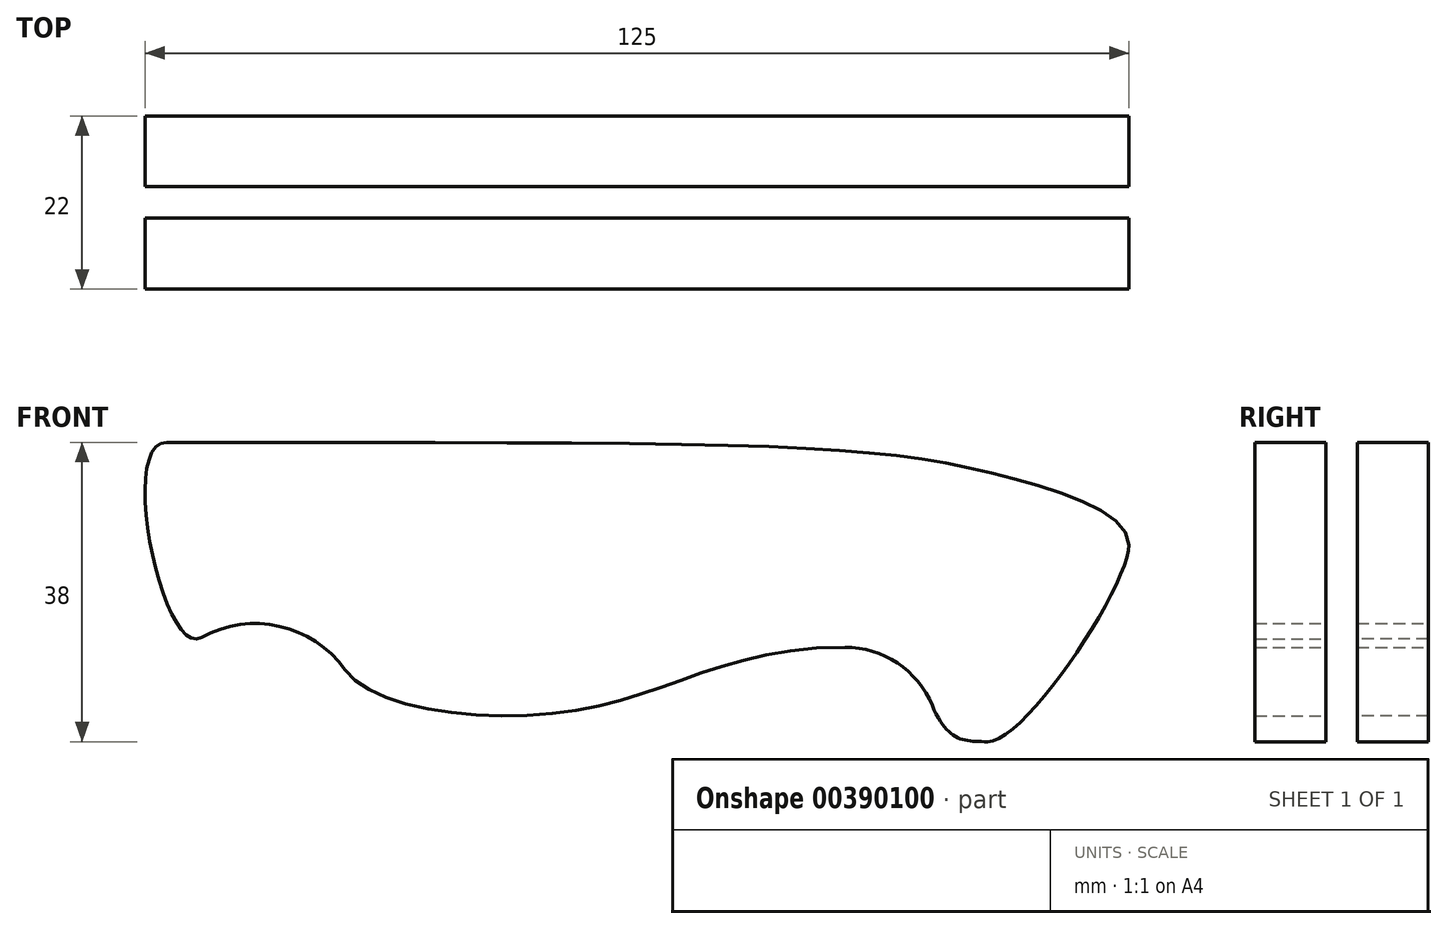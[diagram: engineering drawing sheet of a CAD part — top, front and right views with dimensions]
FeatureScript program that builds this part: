
annotation { "Feature Type Name" : "Feature", "Feature Type Description" : "" }
export const myFeature = defineFeature(function(context is Context, id is Id, definition is map)
    precondition{}
    {
        {
            var Q0;
            Q0=qCreatedBy(makeId("Front.planeOp"),FACE);
            var sketch = newSketch(context, id + "F0", { "sketchPlane" : qUnion([Q0])});
            skLineSegment(sketch, "E0", {"start": v(0, 38) * mm, "end": v(-240, 38) * mm});
            skLineSegment(sketch, "E1", {"start": v(-240, 38) * mm, "end": v(-240, 0) * mm});
            skLineSegment(sketch, "E2", {"start": v(-240, 0) * mm, "end": v(0, 0) * mm});
            skLineSegment(sketch, "E3", {"start": v(0, 0) * mm, "end": v(0, 38) * mm});
            skSolve(sketch);
        }
        {
            var Q0;
            Q0=makeQuery(id+"F0.imprint","IMPRINT",FACE,{"disambiguationData":[TD([[makeQuery(id+"F0.imprint","IMPRINT",EDGE,{"derivedFrom":sQuery(id+"F0.wireOp",EDGE,"E0")}),1.0]])]});
            var sketch = newSketch(context, id + "F1", { "sketchPlane" : qUnion([Q0])});
            skLineSegment(sketch, "E4", {"start": v(0, 50) * mm, "end": v(-125, 50) * mm, "construction": true});
            skLineSegment(sketch, "E5", {"start": v(-125, 50) * mm, "end": v(-240, 50) * mm, "construction": true});
            skLineSegment(sketch, "E6", {"start": v(-125, 50) * mm, "end": v(-125, 0) * mm, "construction": true});
            skLineSegment(sketch, "E7", {"start": v(-240, 0) * mm, "end": v(-240, 30) * mm, "construction": true});
            skLineSegment(sketch, "E8", {"start": v(0, 0) * mm, "end": v(0, 25) * mm, "construction": true});
            skFitSpline(sketch, "E9", {"points": [v(-240, 30) * mm, v(-125, 38) * mm], "startDerivative": vector(108.51, 24) * mm, "endDerivative": vector(182.2, 0) * mm});
            skLineSegment(sketch, "E10", {"start": v(0, 0) * mm, "end": v(-18, 0) * mm, "construction": true});
            skFitSpline(sketch, "E11", {"points": [v(-240, 30) * mm, v(-125, 0) * mm], "startDerivative": vector(22.07, -90) * mm, "endDerivative": vector(212.78, 0) * mm});
            skLineSegment(sketch, "E12", {"start": v(-111, 0) * mm, "end": v(-111, 1) * mm, "construction": true});
            skLineSegment(sketch, "E13", {"start": v(-111, 1) * mm, "end": v(-125, 1) * mm, "construction": true});
            skArc(sketch, "E14", {"start": v(-99.6, 9.13) * mm, "mid": v(-115.27, 14.33) * mm, "end": v(-125, 1) * mm});
            skLineSegment(sketch, "E15", {"start": v(-125, 38) * mm, "end": v(-15, 38) * mm, "construction": true});
            skFitSpline(sketch, "E16", {"points": [v(-125, 38) * mm, v(-15, 33.5) * mm, v(0, 25) * mm], "startDerivative": vector(334.98, 0) * mm, "endDerivative": vector(0, -42.32) * mm});
            skFitSpline(sketch, "E17", {"points": [v(0, 25) * mm, v(-18, 0) * mm], "startDerivative": vector(0, -15) * mm, "endDerivative": vector(-15, 0) * mm});
            skLineSegment(sketch, "E18", {"start": v(-125, 38) * mm, "end": v(-45, 38) * mm, "construction": true});
            skLineSegment(sketch, "E19", {"start": v(0, 29) * mm, "end": v(0, 25) * mm, "construction": true});
            skLineSegment(sketch, "E20", {"start": v(0, 25) * mm, "end": v(0, 20) * mm, "construction": true});
            skLineSegment(sketch, "E21", {"start": v(-18, 0) * mm, "end": v(-13, 0) * mm, "construction": true});
            skLineSegment(sketch, "E22", {"start": v(-125, -8.92) * mm, "end": v(-25, -8.92) * mm, "construction": true});
            skLineSegment(sketch, "E23", {"start": v(-36.08, 0) * mm, "end": v(-36.08, 12) * mm, "construction": true});
            skArc(sketch, "E24", {"start": v(-25, 4.62) * mm, "mid": v(-29.42, 9.98) * mm, "end": v(-36.08, 12) * mm});
            skPoint(sketch, "E25", {"position": v(-99.6, 9.13) * mm});
            skFitSpline(sketch, "E26", {"points": [v(-99.6, 9.13) * mm, v(-70, 4) * mm, v(-36.08, 12) * mm], "startDerivative": vector(23.51, -32.98) * mm, "endDerivative": vector(86.78, 0) * mm});
            skPoint(sketch, "E27", {"position": v(-25, 4.62) * mm});
            skLineSegment(sketch, "E28", {"start": v(-25, 4.62) * mm, "end": v(-23.08, 0) * mm, "construction": true});
            skFitSpline(sketch, "E29", {"points": [v(-18, 0) * mm, v(-25, 4.62) * mm], "startDerivative": vector(-9, 0) * mm, "endDerivative": vector(-5.77, 13.85) * mm});
            skLineSegment(sketch, "E30", {"start": v(-125, 0) * mm, "end": v(-125, 1) * mm});
            skLineSegment(sketch, "E31", {"start": v(-25, -8.92) * mm, "end": v(-25, 4.62) * mm, "construction": true});
            skLineSegment(sketch, "E32", {"start": v(-15, 33.5) * mm, "end": v(-15, 38) * mm, "construction": true});
            skLineSegment(sketch, "E33", {"start": v(-18, 0) * mm, "end": v(-21, 0) * mm, "construction": true});
            skLineSegment(sketch, "E34", {"start": v(-125, -5.42) * mm, "end": v(-70, -5.42) * mm, "construction": true});
            skLineSegment(sketch, "E35", {"start": v(-125, -8.92) * mm, "end": v(-129, -8.92) * mm, "construction": true});
            skLineSegment(sketch, "E36", {"start": v(-129, 0) * mm, "end": v(-129, 38) * mm});
            skLineSegment(sketch, "E37", {"start": v(-111, 1) * mm, "end": v(-99.6, 1) * mm, "construction": true});
            skLineSegment(sketch, "E38", {"start": v(-99.6, 1) * mm, "end": v(-99.6, 9.13) * mm, "construction": true});
            skLineSegment(sketch, "E39", {"start": v(-70, 4) * mm, "end": v(-70, 0) * mm, "construction": true});
            skLineSegment(sketch, "E40", {"start": v(-99.6, 9.13) * mm, "end": v(-95.83, 3.83) * mm, "construction": true});
            skLineSegment(sketch, "E41", {"start": v(-36.08, 12) * mm, "end": v(-51.08, 12) * mm, "construction": true});
            skFitSpline(sketch, "E42", {"points": [v(-122.25, 38) * mm, v(-117.83, 13.22) * mm], "startDerivative": vector(-18.9, 0) * mm, "endDerivative": vector(14.63, 8.17) * mm});
            skLineSegment(sketch, "E43", {"start": v(-117.83, 13.22) * mm, "end": v(-122.7, 10.5) * mm});
            skSolve(sketch);
        }
        {
            var Q0;
            Q0=makeQuery(id+"F1.imprint","IMPRINT",FACE,{"disambiguationData":[TD([[makeQuery(id+"F1.imprint","IMPRINT",EDGE,{"derivedFrom":sQuery(id+"F1.wireOp",EDGE,"E9")}),-1.0]])]});
            extrude(context, id + "F2", {"entities" : qUnion([Q0]), "endBound" : BoundingType.SYMMETRIC, "depth" : 4 * mm});
        }
        {
            var Q0;
            Q0=makeQuery(id+"F2.opExtrude","CAP_EDGE",EDGE,{"disambiguationData":[OSD([sQuery(id+"F1.wireOp",EDGE,"E11")])],"isStart":false});
            var Q1;
            Q1=makeQuery(id+"F2.opExtrude","CAP_EDGE",EDGE,{"disambiguationData":[OSD([sQuery(id+"F1.wireOp",EDGE,"E11")])],"isStart":true});
            chamfer(context, id + "F3", {"entities" : qUnion([Q0, Q1]), "chamferType" : ChamferType.TWO_OFFSETS, "width1" : 20 * mm, "oppositeDirection" : false, "width2" : 2 * mm});
        }
        {
            var Q0;
            Q0=makeQuery(id+"F1.imprint","IMPRINT",FACE,{"disambiguationData":[TD([[makeQuery(id+"F1.imprint","IMPRINT",EDGE,{"derivedFrom":sQuery(id+"F1.wireOp",EDGE,"E14")}),-1.0]])]});
            var Q1;
            {var subQ0=sQuery(id+"F1.wireOp",EDGE,"E17");Q1=makeQuery(id+"F1.imprint","IMPRINT",FACE,{"disambiguationData":[TD([[makeQuery(id+"F1.imprint","IMPRINT",EDGE,{"derivedFrom":subQ0}),-1.0]])]});}
            extrude(context, id + "F4", {"entities" : qUnion([Q0, Q1]), "operationType" : NewBodyOperationType.ADD, "endBound" : BoundingType.SYMMETRIC, "depth" : 4 * mm});
        }
        {
            var Q0;
            {var subQ0=sQuery(id+"F1.wireOp",EDGE,"E17");Q0=makeQuery(id+"F1.imprint","IMPRINT",FACE,{"disambiguationData":[TD([[makeQuery(id+"F1.imprint","IMPRINT",EDGE,{"derivedFrom":subQ0}),-1.0]])]});}
            extrude(context, id + "F5", {"entities" : qUnion([Q0]), "endBound" : BoundingType.SYMMETRIC, "depth" : 22 * mm});
        }
        {
            var Q0;
            Q0=qSketchRegion(id+"F0",true);
            extrude(context, id + "F6", {"entities" : qUnion([Q0]), "operationType" : NewBodyOperationType.REMOVE, "endBound" : BoundingType.SYMMETRIC, "oppositeDirection" : true, "depth" : 4 * mm});
        }
    });
